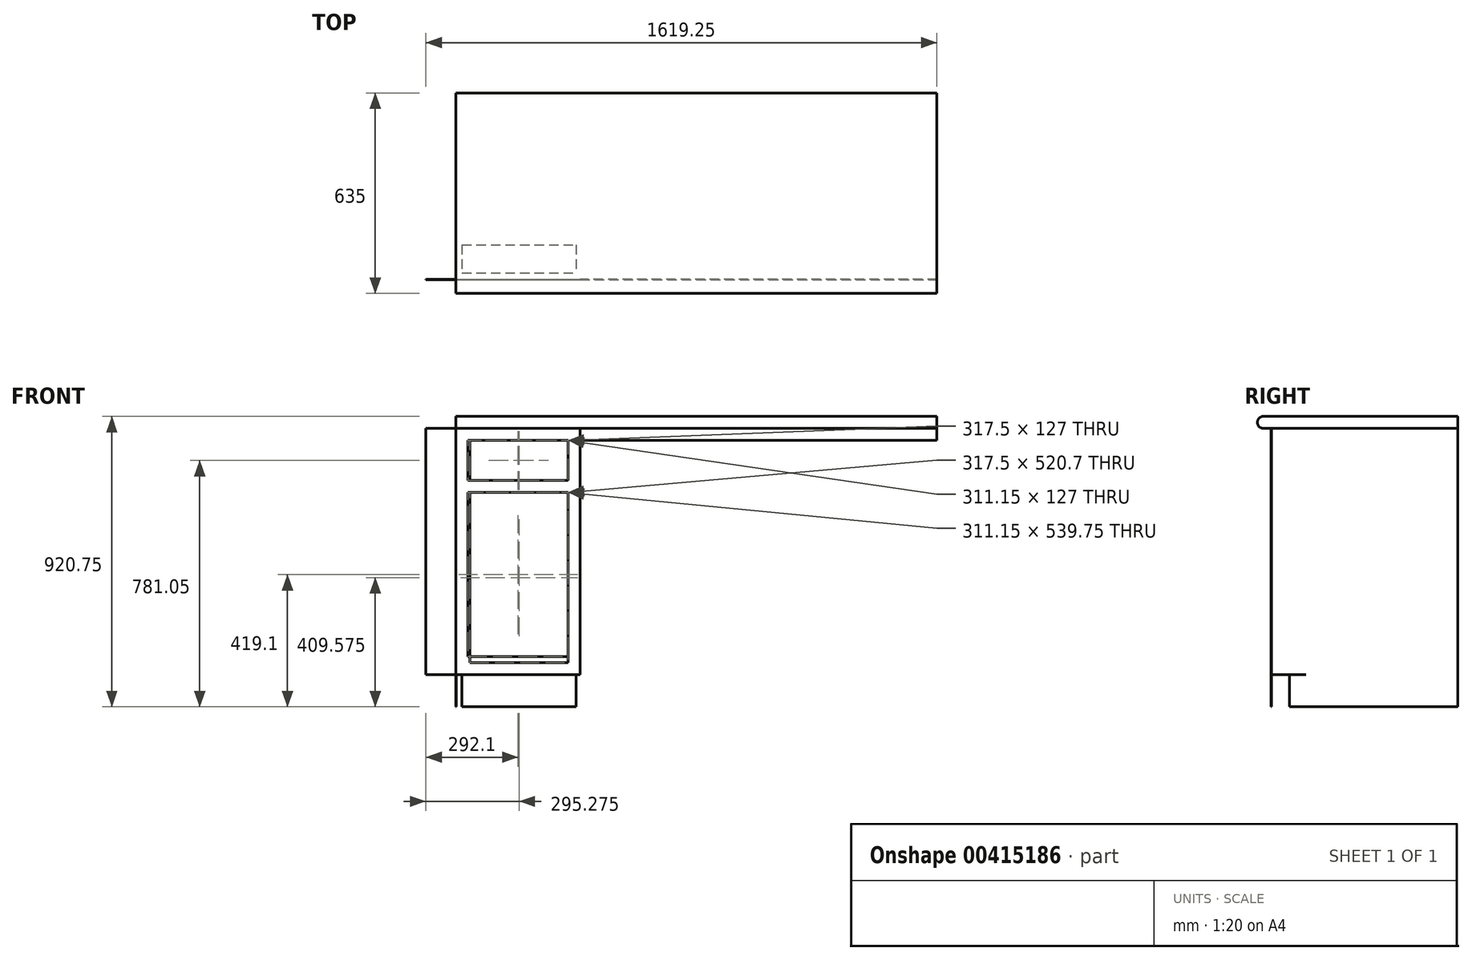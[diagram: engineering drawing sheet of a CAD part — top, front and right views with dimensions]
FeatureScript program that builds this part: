
annotation { "Feature Type Name" : "Feature", "Feature Type Description" : "" }
export const myFeature = defineFeature(function(context is Context, id is Id, definition is map)
    precondition{}
    {
        {
            assignVariable(context, id + "F0", {"name" : "ScribeLeft", "anyValue" : .25});
        }
        {
            assignVariable(context, id + "F1", {"name" : "FrameDepth", "anyValue" : .75});
        }
        {
            assignVariable(context, id + "F2", {"name" : "SideThickness", "anyValue" : .5});
        }
        {
            var Q0;
            Q0=qCreatedBy(makeId("Front.planeOp"),FACE);
            var sketch = newSketch(context, id + "F3", { "sketchPlane" : qUnion([Q0])});
            skLineSegment(sketch, "E0.bottom", {"start": v(0, 0) * mm, "end": v(393.7, 0) * mm});
            skLineSegment(sketch, "E0.top", {"start": v(0, 781.05) * mm, "end": v(393.7, 781.05) * mm});
            skLineSegment(sketch, "E0.left", {"start": v(0, 0) * mm, "end": v(0, 781.05) * mm});
            skLineSegment(sketch, "E0.right", {"start": v(393.7, 0) * mm, "end": v(393.7, 781.05) * mm});
            skLineSegment(sketch, "E1.bottom", {"start": v(38.1, 742.95) * mm, "end": v(355.6, 742.95) * mm});
            skLineSegment(sketch, "E1.top", {"start": v(38.1, 615.95) * mm, "end": v(355.6, 615.95) * mm});
            skLineSegment(sketch, "E1.left", {"start": v(38.1, 742.95) * mm, "end": v(38.1, 615.95) * mm});
            skLineSegment(sketch, "E1.right", {"start": v(355.6, 742.95) * mm, "end": v(355.6, 615.95) * mm});
            skLineSegment(sketch, "E2.bottom", {"start": v(38.1, 577.85) * mm, "end": v(355.6, 577.85) * mm});
            skLineSegment(sketch, "E2.top", {"start": v(38.1, 57.15) * mm, "end": v(355.6, 57.15) * mm});
            skLineSegment(sketch, "E2.left", {"start": v(38.1, 577.85) * mm, "end": v(38.1, 57.15) * mm});
            skLineSegment(sketch, "E2.right", {"start": v(355.6, 577.85) * mm, "end": v(355.6, 57.15) * mm});
            skSolve(sketch);
        }
        {
            var Q0;
            Q0 = qSketchRegion(id + "F3", true);
            extrude(context, id + "F4", {"entities" : qUnion([Q0]), "depth" : (getVariable(context, 'FrameDepth')) * mm});
        }
        {
            var Q0;
            Q0=qCreatedBy(makeId("Right.planeOp"),FACE);
            cPlane(context, id + "F5", {"entities" : qUnion([Q0]), "cplaneType" : CPlaneType.OFFSET, "offset" : (getVariable(context, 'ScribeLeft')) * mm, "width" : 152.4 * mm, "height" : 152.4 * mm});
        }
        {
            var Q0;
            Q0=qCreatedBy(id+"F5.planeOp",FACE);
            var sketch = newSketch(context, id + "F6", { "sketchPlane" : qUnion([Q0])});
            skLineSegment(sketch, "E3.bottom", {"start": v(0, 781.05) * mm, "end": v(590.55, 781.05) * mm});
            skLineSegment(sketch, "E3.top", {"start": v(57.15, -101.6) * mm, "end": v(590.55, -101.6) * mm});
            skLineSegment(sketch, "E3.left", {"start": v(0, 781.05) * mm, "end": v(0, 0) * mm});
            skLineSegment(sketch, "E3.right", {"start": v(590.55, 781.05) * mm, "end": v(590.55, -101.6) * mm});
            skLineSegment(sketch, "E4", {"start": v(0, 0) * mm, "end": v(57.15, 0) * mm});
            skLineSegment(sketch, "E5", {"start": v(57.15, 0) * mm, "end": v(57.15, -101.6) * mm});
            skSolve(sketch);
        }
        {
            var Q0;
            Q0 = qSketchRegion(id + "F6", true);
            extrude(context, id + "F7", {"entities" : qUnion([Q0]), "depth" : (getVariable(context, 'SideThickness')) * mm});
        }
        {
            var Q0;
            Q0=qCreatedBy(makeId("Front.planeOp"),FACE);
            var sketch = newSketch(context, id + "F8", { "sketchPlane" : qUnion([Q0])});
            skLineSegment(sketch, "E6.bottom", {"start": v(19.05, 0) * mm, "end": v(381, 0) * mm});
            skLineSegment(sketch, "E6.top", {"start": v(19.05, -101.6) * mm, "end": v(381, -101.6) * mm});
            skLineSegment(sketch, "E6.left", {"start": v(19.05, 0) * mm, "end": v(19.05, -101.6) * mm});
            skLineSegment(sketch, "E6.right", {"start": v(381, 0) * mm, "end": v(381, -101.6) * mm});
            skSolve(sketch);
        }
        {
            var Q0;
            Q0 = qSketchRegion(id + "F8", true);
            extrude(context, id + "F9", {"entities" : qUnion([Q0]), "depth" : (getVariable(context, 'FrameDepth')) * mm});
        }
        {
            var Q0;
            Q0=qCreatedBy(makeId("Top.planeOp"),FACE);
            var sketch = newSketch(context, id + "F10", { "sketchPlane" : qUnion([Q0])});
            skLineSegment(sketch, "E7.bottom", {"start": v(19.05, 109.34) * mm, "end": v(381, 109.34) * mm});
            skLineSegment(sketch, "E7.top", {"start": v(19.05, 20.44) * mm, "end": v(381, 20.44) * mm});
            skLineSegment(sketch, "E7.left", {"start": v(19.05, 109.34) * mm, "end": v(19.05, 20.44) * mm});
            skLineSegment(sketch, "E7.right", {"start": v(381, 109.34) * mm, "end": v(381, 20.44) * mm});
            skSolve(sketch);
        }
        {
            var Q0;
            Q0 = qSketchRegion(id + "F10", true);
            extrude(context, id + "F11", {"entities" : qUnion([Q0]), "depth" : (getVariable(context, 'FrameDepth')) * mm});
        }
        {
            var Q0;
            Q0=makeQuery(id+"F4.opExtrude","CAP_FACE",FACE,{"disambiguationData":[OSD([sQuery(id+"F3.wireOp",EDGE,"E0.bottom"),sQuery(id+"F3.wireOp",EDGE,"E0.top"),sQuery(id+"F3.wireOp",EDGE,"E0.left"),sQuery(id+"F3.wireOp",EDGE,"E0.right"),sQuery(id+"F3.wireOp",EDGE,"E1.bottom"),sQuery(id+"F3.wireOp",EDGE,"E1.top"),sQuery(id+"F3.wireOp",EDGE,"E1.left"),sQuery(id+"F3.wireOp",EDGE,"E1.right"),sQuery(id+"F3.wireOp",EDGE,"E2.bottom"),sQuery(id+"F3.wireOp",EDGE,"E2.top"),sQuery(id+"F3.wireOp",EDGE,"E2.left"),sQuery(id+"F3.wireOp",EDGE,"E2.right")])],"isStart":false});
            var sketch = newSketch(context, id + "F12", { "sketchPlane" : qUnion([Q0])});
            skLineSegment(sketch, "E8.bottom", {"start": v(393.7, 781.05) * mm, "end": v(1524, 781.05) * mm});
            skLineSegment(sketch, "E8.top", {"start": v(393.7, 742.95) * mm, "end": v(1524, 742.95) * mm});
            skLineSegment(sketch, "E8.left", {"start": v(393.7, 781.05) * mm, "end": v(393.7, 742.95) * mm});
            skLineSegment(sketch, "E8.right", {"start": v(1524, 781.05) * mm, "end": v(1524, 742.95) * mm});
            skSolve(sketch);
        }
        {
            var Q0;
            Q0 = qSketchRegion(id + "F12", true);
            var Q1;
            Q1=makeQuery(id+"F4.opExtrude","CAP_FACE",FACE,{"disambiguationData":[OSD([sQuery(id+"F3.wireOp",EDGE,"E0.bottom"),sQuery(id+"F3.wireOp",EDGE,"E0.top"),sQuery(id+"F3.wireOp",EDGE,"E0.left"),sQuery(id+"F3.wireOp",EDGE,"E0.right"),sQuery(id+"F3.wireOp",EDGE,"E1.bottom"),sQuery(id+"F3.wireOp",EDGE,"E1.top"),sQuery(id+"F3.wireOp",EDGE,"E1.left"),sQuery(id+"F3.wireOp",EDGE,"E1.right"),sQuery(id+"F3.wireOp",EDGE,"E2.bottom"),sQuery(id+"F3.wireOp",EDGE,"E2.top"),sQuery(id+"F3.wireOp",EDGE,"E2.left"),sQuery(id+"F3.wireOp",EDGE,"E2.right")])],"isStart":true});
            extrude(context, id + "F13", {"entities" : qUnion([Q0]), "endBound" : BoundingType.UP_TO_SURFACE, "oppositeDirection" : true, "depth" : 25.4 * mm, "endBoundEntityFace" : qUnion([Q1]), "offsetDistance" : 25.4 * mm});
        }
        {
            var Q0;
            Q0=makeQuery(id+"F4.opExtrude","SWEPT_FACE",FACE,{"disambiguationData":[OSD([sQuery(id+"F3.wireOp",EDGE,"E0.top")])]});
            var sketch = newSketch(context, id + "F14", { "sketchPlane" : qUnion([Q0])});
            skLineSegment(sketch, "E9.bottom", {"start": v(0, 590.55) * mm, "end": v(1524, 590.55) * mm});
            skLineSegment(sketch, "E9.top", {"start": v(0, -44.45) * mm, "end": v(1524, -44.45) * mm});
            skLineSegment(sketch, "E9.left", {"start": v(0, 590.55) * mm, "end": v(0, -44.45) * mm});
            skLineSegment(sketch, "E9.right", {"start": v(1524, 590.55) * mm, "end": v(1524, -44.45) * mm});
            skSolve(sketch);
        }
        {
            var Q0;
            Q0 = qSketchRegion(id + "F14", true);
            extrude(context, id + "F15", {"entities" : qUnion([Q0]), "depth" : 38.1 * mm, "offsetDistance" : 25.4 * mm});
        }
        {
            var Q0;
            Q0=makeQuery(id+"F15.opExtrude","CAP_EDGE",EDGE,{"disambiguationData":[OSD([sQuery(id+"F14.wireOp",EDGE,"E9.top")])],"isStart":false});
            var Q1;
            Q1=makeQuery(id+"F15.opExtrude","CAP_EDGE",EDGE,{"disambiguationData":[OSD([sQuery(id+"F14.wireOp",EDGE,"E9.top")])],"isStart":true});
            fillet(context, id + "F16", {"entities" : qUnion([Q0, Q1]), "radius" : 19.05 * mm, "tangentPropagation" : true, "allowEdgeOverflow" : false});
        }
        {
            var Q0;
            Q0=makeQuery(id+"F7.opExtrude","SWEPT_FACE",FACE,{"disambiguationData":[OSD([sQuery(id+"F6.wireOp",EDGE,"E3.left")])]});
            var sketch = newSketch(context, id + "F17", { "sketchPlane" : qUnion([Q0])});
            skLineSegment(sketch, "E10.bottom", {"start": v(-95.25, 781.05) * mm, "end": v(393.7, 781.05) * mm});
            skLineSegment(sketch, "E10.top", {"start": v(-95.25, 0) * mm, "end": v(393.7, 0) * mm});
            skLineSegment(sketch, "E10.left", {"start": v(-95.25, 781.05) * mm, "end": v(-95.25, 0) * mm});
            skLineSegment(sketch, "E10.right", {"start": v(393.7, 781.05) * mm, "end": v(393.7, 0) * mm});
            skLineSegment(sketch, "E11", {"start": v(0, 781.05) * mm, "end": v(0, 0) * mm, "construction": true});
            skLineSegment(sketch, "E12.bottom", {"start": v(44.45, 742.95) * mm, "end": v(355.6, 742.95) * mm});
            skLineSegment(sketch, "E12.top", {"start": v(44.45, 615.95) * mm, "end": v(355.6, 615.95) * mm});
            skLineSegment(sketch, "E12.left", {"start": v(44.45, 742.95) * mm, "end": v(44.45, 615.95) * mm});
            skLineSegment(sketch, "E12.right", {"start": v(355.6, 742.95) * mm, "end": v(355.6, 615.95) * mm});
            skLineSegment(sketch, "E13.bottom", {"start": v(44.45, 577.85) * mm, "end": v(355.6, 577.85) * mm});
            skLineSegment(sketch, "E13.top", {"start": v(44.45, 38.1) * mm, "end": v(355.6, 38.1) * mm});
            skLineSegment(sketch, "E13.left", {"start": v(44.45, 577.85) * mm, "end": v(44.45, 38.1) * mm});
            skLineSegment(sketch, "E13.right", {"start": v(355.6, 577.85) * mm, "end": v(355.6, 38.1) * mm});
            skSolve(sketch);
        }
        {
            var Q0;
            Q0 = qSketchRegion(id + "F17", true);
            extrude(context, id + "F18", {"entities" : qUnion([Q0]), "depth" : (getVariable(context, 'FrameDepth')) * mm, "offsetDistance" : 25.4 * mm});
        }
    });
